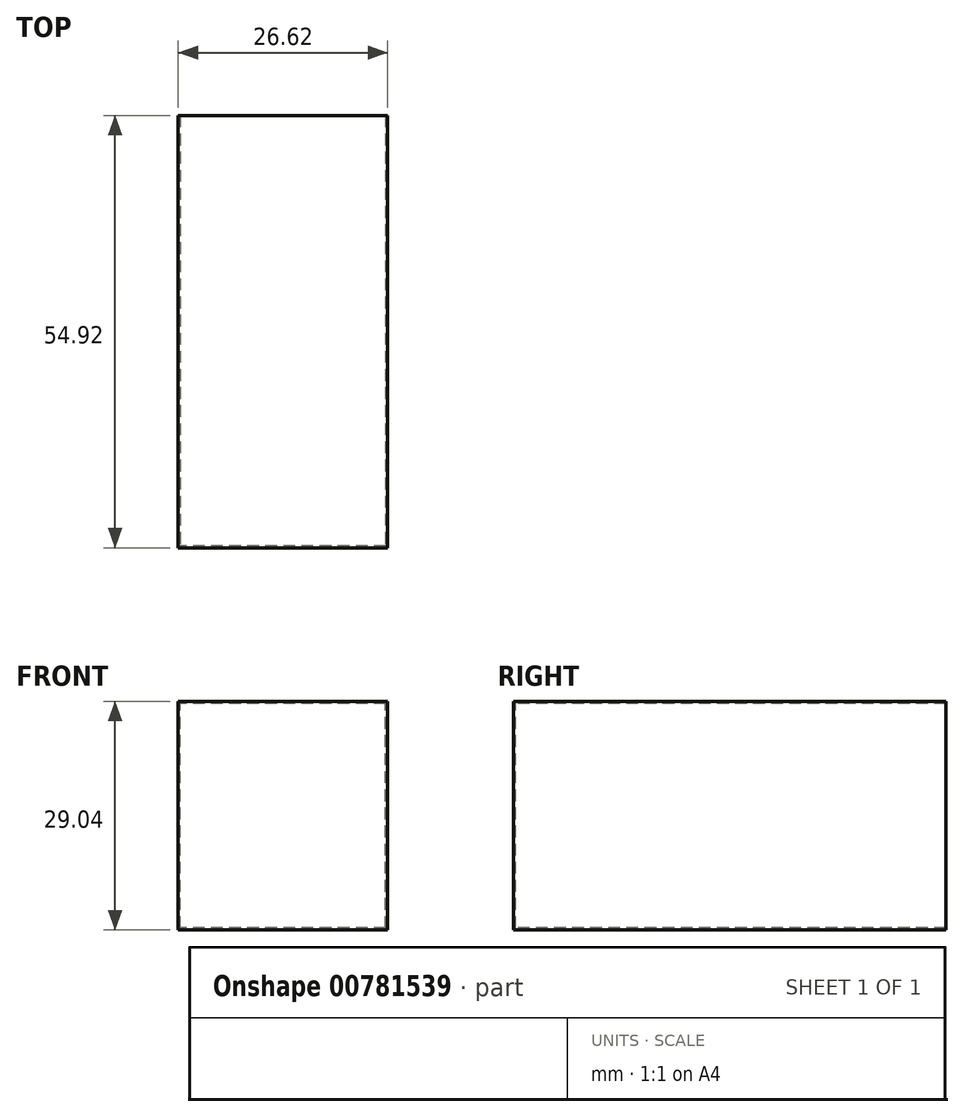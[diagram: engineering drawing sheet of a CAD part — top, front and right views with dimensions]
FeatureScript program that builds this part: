
annotation { "Feature Type Name" : "Feature", "Feature Type Description" : "" }
export const myFeature = defineFeature(function(context is Context, id is Id, definition is map)
    precondition{}
    {
        {
            var Q0;
            Q0=qCreatedBy(makeId("Front.planeOp"),FACE);
            var sketch = newSketch(context, id + "F0", { "sketchPlane" : qUnion([Q0])});
            skLineSegment(sketch, "E0.bottom", {"start": v(13.3, -14.52) * mm, "end": v(-13.3, -14.52) * mm});
            skLineSegment(sketch, "E0.top", {"start": v(13.3, 14.52) * mm, "end": v(-13.3, 14.52) * mm});
            skLineSegment(sketch, "E0.left", {"start": v(13.3, -14.52) * mm, "end": v(13.3, 14.52) * mm});
            skLineSegment(sketch, "E0.right", {"start": v(-13.3, -14.52) * mm, "end": v(-13.3, 14.52) * mm});
            skPoint(sketch, "E0.middle", {"position": v(0, 0) * mm});
            skSolve(sketch);
        }
        {
            var Q0;
            Q0=makeQuery(id+"F0.imprint","IMPRINT",FACE,{"disambiguationData":[TD([[makeQuery(id+"F0.imprint","IMPRINT",EDGE,{"derivedFrom":sQuery(id+"F0.wireOp",EDGE,"E0.bottom")}),-1.0]])]});
            extrude(context, id + "F1", {"entities" : qUnion([Q0]), "oppositeDirection" : true, "depth" : 54.92 * mm, "offsetDistance" : 25.4 * mm});
        }
        {
            var Q0;
            Q0=makeQuery(id+"F1.opExtrude","CAP_FACE",FACE,{"disambiguationData":[OSD([sQuery(id+"F0.wireOp",EDGE,"E0.bottom"),sQuery(id+"F0.wireOp",EDGE,"E0.top"),sQuery(id+"F0.wireOp",EDGE,"E0.left"),sQuery(id+"F0.wireOp",EDGE,"E0.right")])],"isStart":false});
            shell(context, id + "F2", {"entities" : qUnion([Q0]), "thickness" : 0.25 * mm});
        }
    });
